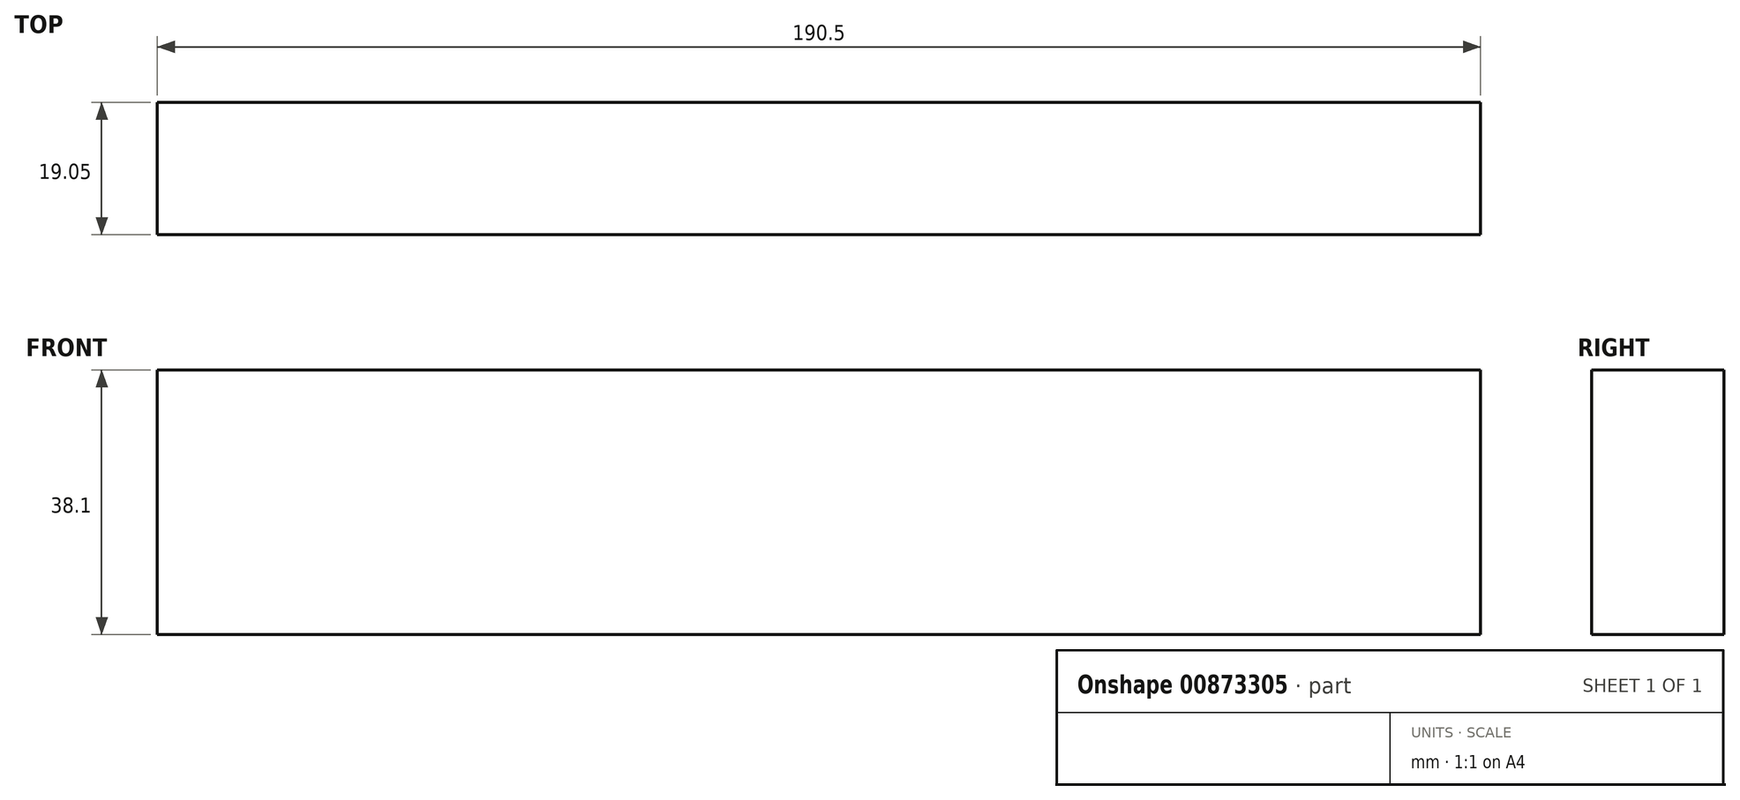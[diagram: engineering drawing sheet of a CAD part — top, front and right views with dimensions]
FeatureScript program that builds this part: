
annotation { "Feature Type Name" : "Feature", "Feature Type Description" : "" }
export const myFeature = defineFeature(function(context is Context, id is Id, definition is map)
    precondition{}
    {
        {
            var Q0;
            Q0=qCreatedBy(makeId("Front.planeOp"),FACE);
            var sketch = newSketch(context, id + "F0", { "sketchPlane" : qUnion([Q0])});
            skLineSegment(sketch, "E0.bottom", {"start": v(0, 0) * mm, "end": v(-190.5, 0) * mm});
            skLineSegment(sketch, "E0.top", {"start": v(0, 38.1) * mm, "end": v(-190.5, 38.1) * mm});
            skLineSegment(sketch, "E0.left", {"start": v(0, 0) * mm, "end": v(0, 38.1) * mm});
            skLineSegment(sketch, "E0.right", {"start": v(-190.5, 0) * mm, "end": v(-190.5, 38.1) * mm});
            skSolve(sketch);
        }
        {
            var Q0;
            Q0=qSketchRegion(id+"F0",true);
            extrude(context, id + "F1", {"entities" : qUnion([Q0]), "depth" : 19.05 * mm, "offsetDistance" : 25.4 * mm});
        }
    });
